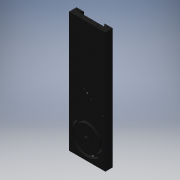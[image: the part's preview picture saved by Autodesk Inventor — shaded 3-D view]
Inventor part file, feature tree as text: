
AUTODESK INVENTOR PART (.ipt)
format: ipt  version: 2016 (Build 200138000, 138)  size: 229,376 bytes
history: native  units: mm
features: extrude x8, sketch x7, reference x5, hole x3, thread x1
ambient origin geometry x8: Origin, YZ Plane, XZ Plane, XY Plane, X Axis, Y Axis, Z Axis, Center Point
bodies: Solid1 (feature_tree)
feature tree (24):
  extrude  "Extrusion1"  Depth=29.6mm
  sketch  "Sketch2"  dims[d2=29.9mm d4=22.68928mm]
  sketch  "Sketch3"  dims[d5=33.0mm d6=8.726646mm]
  extrude  "Extrusion2"  Depth=22.68928mm
  extrude  "Extrusion3"  Depth=8.726646mm
  extrude  "Extrusion4"  Depth=486.0mm
  sketch  "Sketch4"  dims[d7=486.0mm d8=0.0mm d9=22.0mm]
  extrude  "Extrusion5"  Depth=14.5mm
  extrude  "Extrusion7"  Depth=62.1mm
  extrude  "Extrusion8"  Depth=20.0mm
  sketch  "Sketch5"  dims[d10=124.2mm d11=14.5mm]
  sketch  "Sketch6"  dims[d12=62.1mm d13=104.0mm]
  hole  "Hole1"  [1 undecoded]
  hole  "Hole2"  [1 undecoded]
  hole  "Hole3"  [1 undecoded]
  thread  "Thread1"  [1 undecoded]
  extrude  "Extrusion9"  Depth=3.7mm TaperAngle=0.0deg
  sketch  "Sketch1"  dims[d0=146.0mm d1=29.6mm]
  sketch  "Sketch12"  dims[d14=19.02mm d15=8.2mm d17=13.0mm d18=0.0mm d19=7.5mm d20=0.0mm d21=7.5mm d22=0.0mm d23=19.0mm d24=3.7mm d25=0.0mm d26=9.4mm d29=0.0mm d30=18.7mm d31=18.7mm d36=6.0mm d37=0.0mm d38=17.0mm d39=46.5mm d40=3.0mm d41=0.0mm d42=10.0mm d43=225.0mm d44=60.0mm d45=11.0mm d46=60.5mm d47=250.5mm d48=11.0mm d49=190.5mm d50=11.5mm d51=8.5mm d52=6.0mm d53=11.0mm d54=8.5mm d55=90.0deg d56=8.0mm d57=20.594885mm d58=7.0mm d59=6.0mm d60=10.0mm d61=7.5mm d62=90.0deg d63=8.0mm d64=20.594885mm d65=7.5mm d66=6.0mm d67=11.0mm d68=7.0mm d69=90.0deg d70=8.0mm d71=20.594885mm d75=10.0mm d76=0.0mm d77=20.0mm d78=0.0mm]
  reference  "Reference1"
  reference  "Reference2"
  reference  "Reference3"
  reference  "Reference4"
  reference  "Reference5"
note: 4 required parameter values undecoded (feature->parameter linkage not recoverable at this tier; creation-order binding heuristic only, values carry confidence <= 0.55)
